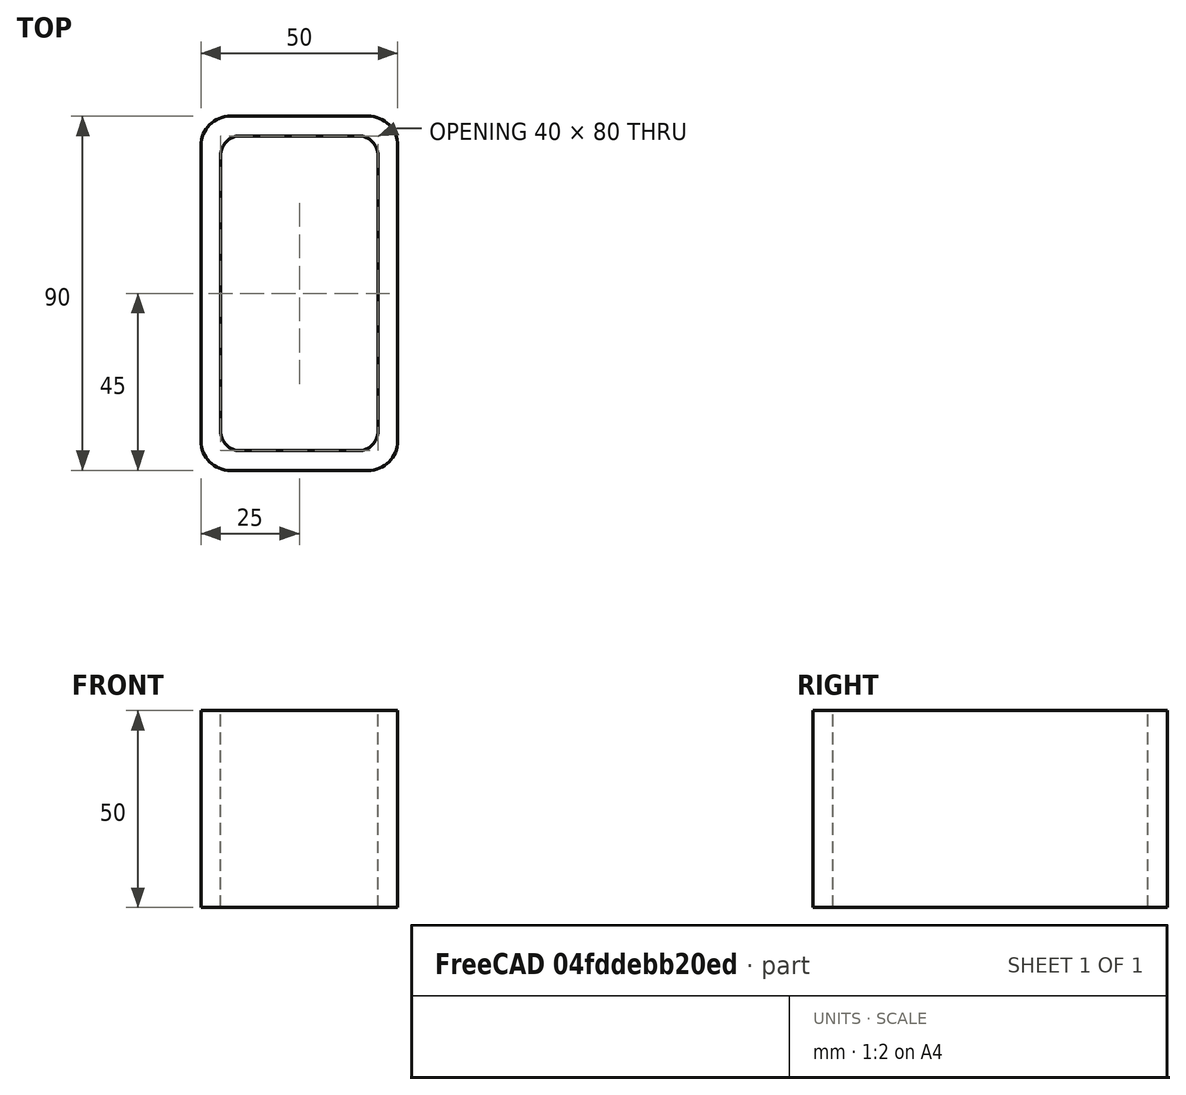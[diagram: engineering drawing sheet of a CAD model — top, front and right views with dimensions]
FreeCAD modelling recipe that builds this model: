
FCSTD DOCUMENT  (FreeCAD 0.15R4671 (Git))
Label: Rectangular hollow section 90x50x5 EN10219 S235JRH
License: All rights reserved
LicenseURL: http://en.wikipedia.org/wiki/All_rights_reserved
objects: Sketcher::SketchObject×1, Part::Extrusion×1
note: 2 computed .brp shape members not serialized (recipe doc carries the construction recipe); baked Part::Feature solids carry a one-line shape summary decoded from their .brp

FEATURE [Sketcher::SketchObject] Sketch
  sketch-geometry (16):
    g0: LineSegment StartX=-15 StartY=40 StartZ=0 EndX=15 EndY=40 EndZ=0
    g1: LineSegment StartX=20 StartY=35 StartZ=0 EndX=20 EndY=-35 EndZ=0
    g2: LineSegment StartX=15 StartY=-40 StartZ=0 EndX=-15 EndY=-40 EndZ=0
    g3: LineSegment StartX=-20 StartY=-35 StartZ=0 EndX=-20 EndY=35 EndZ=0
    g4: LineSegment StartX=-17.5 StartY=45 StartZ=0 EndX=17.5 EndY=45 EndZ=0
    g5: LineSegment StartX=25 StartY=37.5 StartZ=0 EndX=25 EndY=-37.5 EndZ=0
    g6: LineSegment StartX=17.5 StartY=-45 StartZ=0 EndX=-17.5 EndY=-45 EndZ=0
    g7: LineSegment StartX=-25 StartY=-37.5 StartZ=0 EndX=-25 EndY=37.5 EndZ=0
    g8: ArcOfCircle CenterX=-15 CenterY=35 CenterZ=0 NormalX=0 NormalY=0 NormalZ=1 Radius=5 StartAngle=1.5708 EndAngle=3.14159
    g9: ArcOfCircle CenterX=15 CenterY=35 CenterZ=0 NormalX=0 NormalY=0 NormalZ=1 Radius=5 StartAngle=0 EndAngle=1.5708
    g10: ArcOfCircle CenterX=15 CenterY=-35 CenterZ=0 NormalX=0 NormalY=0 NormalZ=1 Radius=5 StartAngle=4.71239 EndAngle=6.28319
    g11: ArcOfCircle CenterX=-15 CenterY=-35 CenterZ=0 NormalX=0 NormalY=0 NormalZ=1 Radius=5 StartAngle=3.14159 EndAngle=4.71239
    g12: ArcOfCircle CenterX=17.5 CenterY=37.5 CenterZ=0 NormalX=0 NormalY=0 NormalZ=1 Radius=7.5 StartAngle=0 EndAngle=1.5708
    g13: ArcOfCircle CenterX=17.5 CenterY=-37.5 CenterZ=0 NormalX=0 NormalY=0 NormalZ=1 Radius=7.5 StartAngle=4.71239 EndAngle=6.28319
    g14: ArcOfCircle CenterX=-17.5 CenterY=-37.5 CenterZ=0 NormalX=0 NormalY=0 NormalZ=1 Radius=7.5 StartAngle=3.14159 EndAngle=4.71239
    g15: ArcOfCircle CenterX=-17.5 CenterY=37.5 CenterZ=0 NormalX=0 NormalY=0 NormalZ=1 Radius=7.5 StartAngle=1.5708 EndAngle=3.14159
  constraints (36):
    c: Horizontal(g2)
    c: Vertical(g3)
    c: Horizontal(g6)
    c: Vertical(g7)
    c: Tangent(g3,g8) = 1.5708
    c: Tangent(g0,g8) = 1.5708
    c: Tangent(g0,g9) = 1.5708
    c: Tangent(g1,g9) = 1.5708
    c: Tangent(g1,g10) = 1.5708
    c: Tangent(g2,g10) = 1.5708
    c: Tangent(g2,g11) = 1.5708
    c: Tangent(g3,g11) = 1.5708
    c: Tangent(g4,g12) = 1.5708
    c: Tangent(g5,g12) = 1.5708
    c: Tangent(g5,g13) = 1.5708
    c: Tangent(g6,g13) = 1.5708
    c: Tangent(g6,g14) = 1.5708
    c: Tangent(g7,g14) = 1.5708
    c: Tangent(g7,g15) = 1.5708
    c: Tangent(g4,g15) = 1.5708
    c: Equal(g9,g8)
    c: Equal(g9,g11)
    c: Equal(g9,g10)
    c: Equal(g12,g15)
    c: Equal(g12,g14)
    c: Equal(g12,g13)
    c: Symmetric(g4,g6,g-1)
    c: Symmetric(g7,g5,g-2)
    c: DistanceY(g4,g6) = -90
    c: DistanceX(g7,g5) = 50
    c: Symmetric(g3,g1,g-2)
    c: Symmetric(g0,g2,g-1)
    c: DistanceY(g0,g4) = 5
    c: DistanceX(g5,g1) = -5
    c: Radius(g9) = 5
    c: Radius(g12) = 7.5
FEATURE [Part::Extrusion] Extrude  label="Rectangular hollow section 90x50x5 EN10219 S235JRH"
  Base = -> Sketch
  Dir = (0,0,50)
  Solid = true
